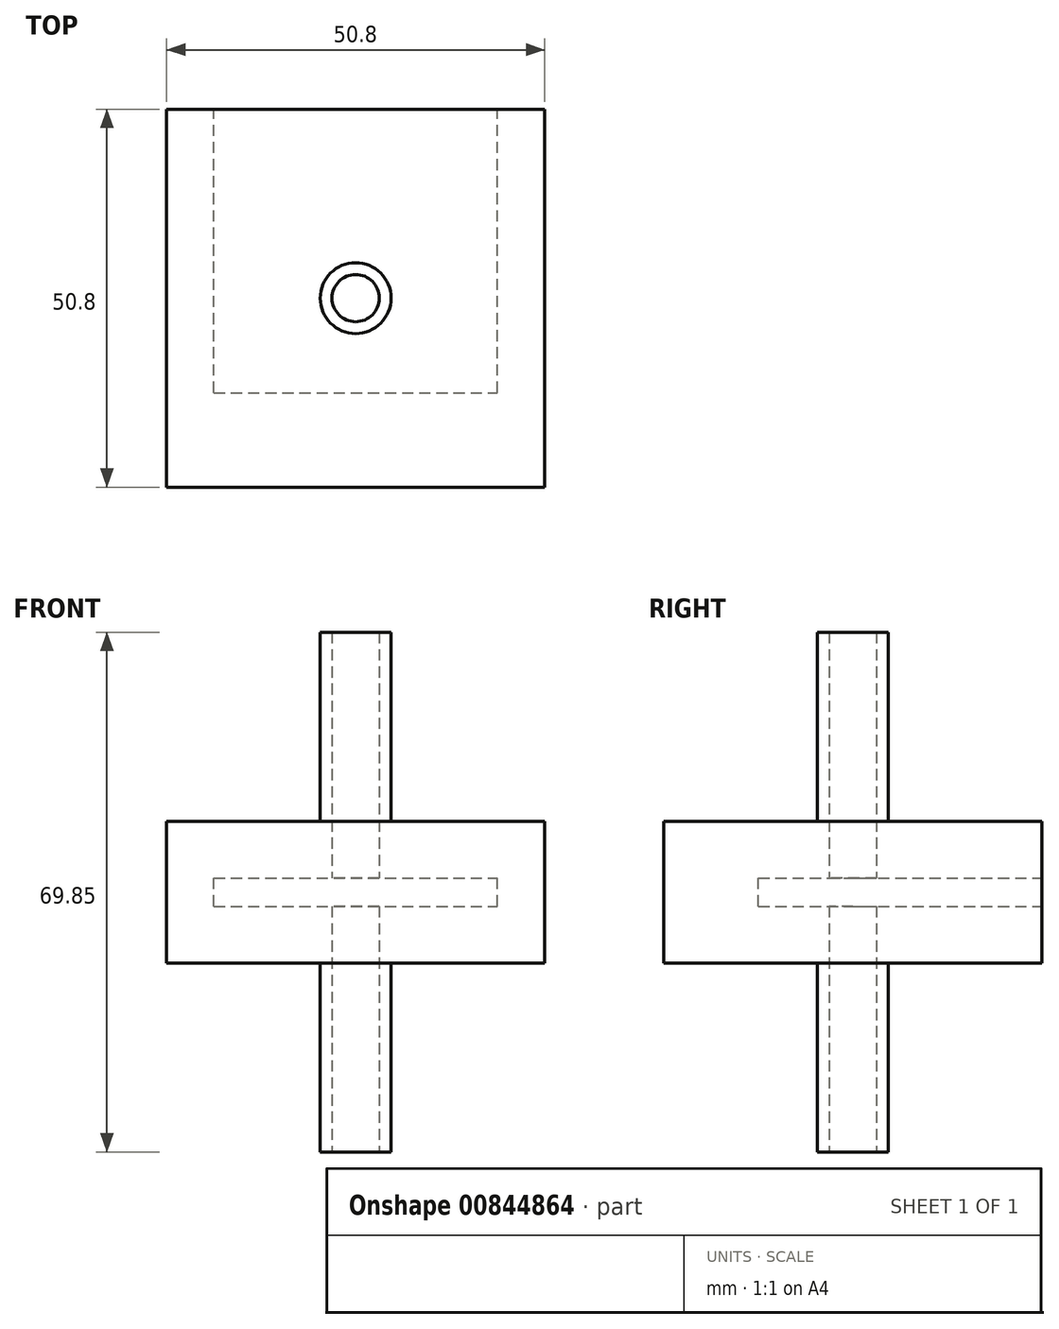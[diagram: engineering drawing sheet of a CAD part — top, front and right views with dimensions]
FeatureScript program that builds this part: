
annotation { "Feature Type Name" : "Feature", "Feature Type Description" : "" }
export const myFeature = defineFeature(function(context is Context, id is Id, definition is map)
    precondition{}
    {
        {
            var Q0;
            Q0=qCreatedBy(makeId("Top.planeOp"),FACE);
            var sketch = newSketch(context, id + "F0", { "sketchPlane" : qUnion([Q0])});
            skLineSegment(sketch, "E0.bottom", {"start": v(25.4, 25.4) * mm, "end": v(-25.4, 25.4) * mm});
            skLineSegment(sketch, "E0.top", {"start": v(25.4, -25.4) * mm, "end": v(-25.4, -25.4) * mm});
            skLineSegment(sketch, "E0.left", {"start": v(25.4, 25.4) * mm, "end": v(25.4, -25.4) * mm});
            skLineSegment(sketch, "E0.right", {"start": v(-25.4, 25.4) * mm, "end": v(-25.4, -25.4) * mm});
            skPoint(sketch, "E0.middle", {"position": v(0, 0) * mm});
            skSolve(sketch);
        }
        {
            var Q0;
            Q0 = qSketchRegion(id + "F0", true);
            extrude(context, id + "F1", {"entities" : qUnion([Q0]), "depth" : 19.05 * mm, "offsetDistance" : 25.4 * mm});
        }
        {
            var Q0;
            Q0=makeQuery(id+"F1.opExtrude","SWEPT_FACE",FACE,{"disambiguationData":[OSD([sQuery(id+"F0.wireOp",EDGE,"E0.bottom")])]});
            var sketch = newSketch(context, id + "F2", { "sketchPlane" : qUnion([Q0])});
            skLineSegment(sketch, "E1.bottom", {"start": v(19.05, 7.62) * mm, "end": v(-19.05, 7.62) * mm});
            skLineSegment(sketch, "E1.top", {"start": v(19.05, 11.43) * mm, "end": v(-19.05, 11.43) * mm});
            skLineSegment(sketch, "E1.left", {"start": v(19.05, 7.62) * mm, "end": v(19.05, 11.43) * mm});
            skLineSegment(sketch, "E1.right", {"start": v(-19.05, 7.62) * mm, "end": v(-19.05, 11.43) * mm});
            skPoint(sketch, "E1.middle", {"position": v(0, 9.53) * mm});
            skSolve(sketch);
        }
        {
            var Q0;
            Q0=makeQuery(id+"F2.imprint","IMPRINT",FACE,{"disambiguationData":[TD([[makeQuery(id+"F2.imprint","IMPRINT",EDGE,{"derivedFrom":sQuery(id+"F2.wireOp",EDGE,"E1.bottom")}),-1.0]])]});
            extrude(context, id + "F3", {"entities" : qUnion([Q0]), "operationType" : NewBodyOperationType.REMOVE, "oppositeDirection" : true, "depth" : 38.1 * mm, "offsetDistance" : 25.4 * mm});
        }
        {
            var Q0;
            Q0=makeQuery(id+"F1.opExtrude","CAP_FACE",FACE,{"disambiguationData":[OSD([sQuery(id+"F0.wireOp",EDGE,"E0.bottom"),sQuery(id+"F0.wireOp",EDGE,"E0.top"),sQuery(id+"F0.wireOp",EDGE,"E0.left"),sQuery(id+"F0.wireOp",EDGE,"E0.right")])],"isStart":false});
            var sketch = newSketch(context, id + "F4", { "sketchPlane" : qUnion([Q0])});
            skSolve(sketch);
        }
        {
            var Q0;
            Q0=makeQuery(id+"F4.imprint","IMPRINT",FACE,{"disambiguationData":[TD([[makeQuery(id+"F4.imprint","IMPRINT",EDGE,{"derivedFrom":makeQuery(id+"F1.opExtrude","CAP_EDGE",EDGE,{"disambiguationData":[OSD([sQuery(id+"F0.wireOp",EDGE,"E0.bottom")])],"isStart":false})}),1.0]])]});
            var sketch = newSketch(context, id + "F5", { "sketchPlane" : qUnion([Q0])});
            skCircle(sketch, "E2", {"center": v(0, 0) * mm, "radius": 4.76 * mm});
            skSolve(sketch);
        }
        {
            var Q0;
            Q0 = qSketchRegion(id + "F5", true);
            var Q1;
            Q1=sQuery(id+"F5.wireOp",EDGE,"E2");
            extrude(context, id + "F6", {"entities" : qUnion([Q0]), "operationType" : NewBodyOperationType.ADD, "surfaceOperationType" : NewSurfaceOperationType.ADD, "surfaceEntities" : qUnion([Q1]), "depth" : 25.4 * mm, "offsetDistance" : 25.4 * mm});
        }
        {
            var Q0;
            Q0=makeQuery(id+"F1.opExtrude","CAP_FACE",FACE,{"disambiguationData":[OSD([sQuery(id+"F0.wireOp",EDGE,"E0.bottom"),sQuery(id+"F0.wireOp",EDGE,"E0.top"),sQuery(id+"F0.wireOp",EDGE,"E0.left"),sQuery(id+"F0.wireOp",EDGE,"E0.right")])],"isStart":true});
            var sketch = newSketch(context, id + "F7", { "sketchPlane" : qUnion([Q0])});
            skCircle(sketch, "E3", {"center": v(0, 0) * mm, "radius": 4.76 * mm});
            skSolve(sketch);
        }
        {
            var Q0;
            Q0=makeQuery(id+"F7.imprint","IMPRINT",FACE,{"disambiguationData":[TD([[makeQuery(id+"F7.imprint","IMPRINT",EDGE,{"derivedFrom":sQuery(id+"F7.wireOp",EDGE,"E3")}),1.0]])]});
            var Q1;
            Q1=sQuery(id+"F7.wireOp",EDGE,"E3");
            extrude(context, id + "F8", {"entities" : qUnion([Q0]), "operationType" : NewBodyOperationType.ADD, "surfaceEntities" : qUnion([Q1]), "depth" : 25.4 * mm, "offsetDistance" : 25.4 * mm});
        }
        {
            var Q0;
            Q0=makeQuery(id+"F8.opExtrude","CAP_FACE",FACE,{"disambiguationData":[OSD([sQuery(id+"F7.wireOp",EDGE,"E3")])],"isStart":false});
            var sketch = newSketch(context, id + "F9", { "sketchPlane" : qUnion([Q0])});
            skCircle(sketch, "E4", {"center": v(0, 0) * mm, "radius": 3.17 * mm});
            skSolve(sketch);
        }
        {
            var Q0;
            Q0 = qSketchRegion(id + "F9", true);
            extrude(context, id + "F10", {"entities" : qUnion([Q0]), "operationType" : NewBodyOperationType.REMOVE, "oppositeDirection" : true, "depth" : 74.68 * mm, "offsetDistance" : 25.4 * mm});
        }
    });
